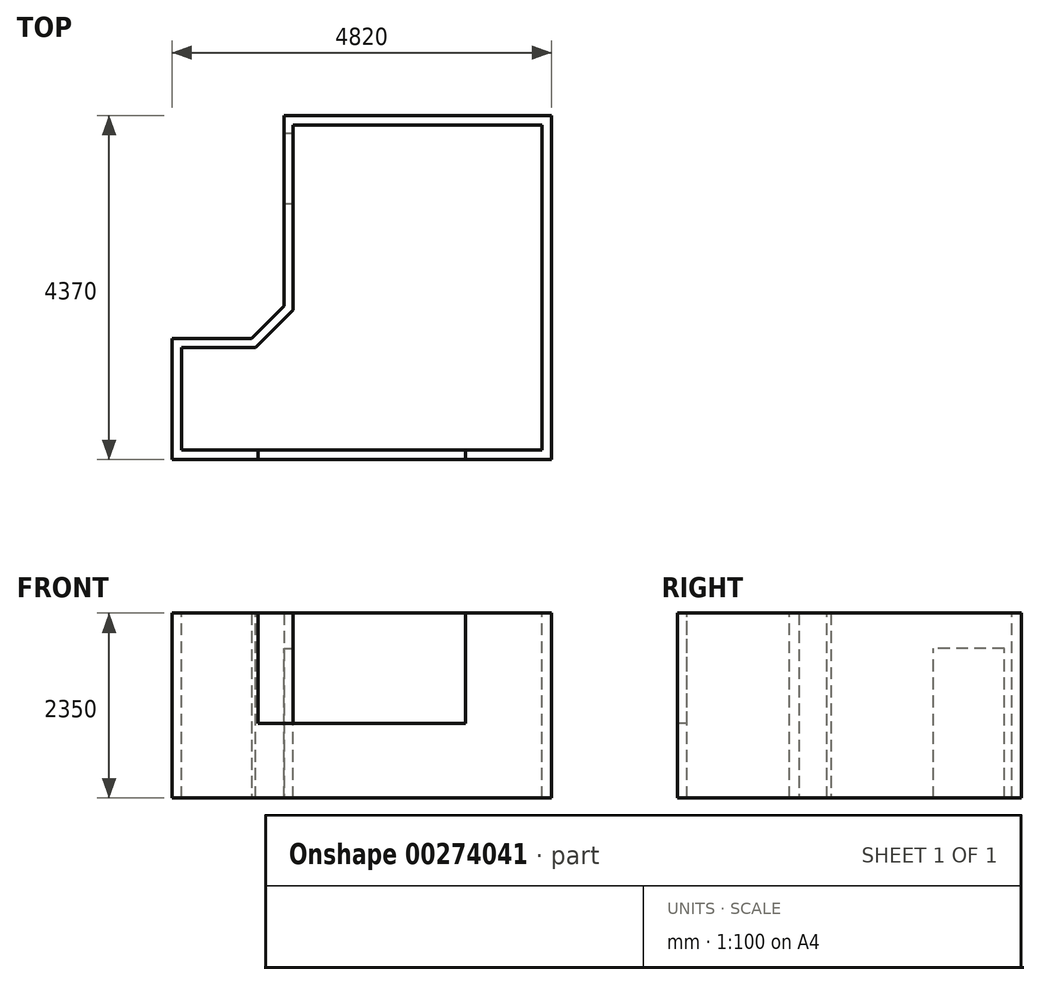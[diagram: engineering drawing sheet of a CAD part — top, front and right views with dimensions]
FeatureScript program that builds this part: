
annotation { "Feature Type Name" : "Feature", "Feature Type Description" : "" }
export const myFeature = defineFeature(function(context is Context, id is Id, definition is map)
    precondition{}
    {
        {
            var Q0;
            Q0=qCreatedBy(makeId("Top.planeOp"),FACE);
            var sketch = newSketch(context, id + "F0", { "sketchPlane" : qUnion([Q0])});
            skLineSegment(sketch, "E0", {"start": v(-2410, -1135) * mm, "end": v(-2410, -2675) * mm});
            skLineSegment(sketch, "E1", {"start": v(-2410, -2675) * mm, "end": v(2410, -2675) * mm});
            skLineSegment(sketch, "E2", {"start": v(2410, -2675) * mm, "end": v(2410, 1695) * mm});
            skLineSegment(sketch, "E3", {"start": v(2410, 1695) * mm, "end": v(-990, 1695) * mm});
            skLineSegment(sketch, "E4", {"start": v(-990, 1695) * mm, "end": v(-990, -725.9) * mm});
            skLineSegment(sketch, "E5", {"start": v(-990, -725.9) * mm, "end": v(-1399.1, -1135) * mm});
            skLineSegment(sketch, "E6", {"start": v(-1399.1, -1135) * mm, "end": v(-2410, -1135) * mm});
            skSolve(sketch);
        }
        {
            var Q0;
            Q0=qSketchRegion(id+"F0",true);
            extrude(context, id + "F1", {"entities" : qUnion([Q0]), "depth" : 2350 * mm});
        }
        {
            var Q0;
            Q0=makeQuery(id+"F1.opExtrude","CAP_FACE",FACE,{"disambiguationData":[OSD([sQuery(id+"F0.wireOp",EDGE,"E0"),sQuery(id+"F0.wireOp",EDGE,"E1"),sQuery(id+"F0.wireOp",EDGE,"E2"),sQuery(id+"F0.wireOp",EDGE,"E3"),sQuery(id+"F0.wireOp",EDGE,"E4"),sQuery(id+"F0.wireOp",EDGE,"E5"),sQuery(id+"F0.wireOp",EDGE,"E6")])],"isStart":false});
            var sketch = newSketch(context, id + "F2", { "sketchPlane" : qUnion([Q0])});
            skLineSegment(sketch, "E7", {"start": v(-2290, -1255) * mm, "end": v(-2290, -2555) * mm});
            skLineSegment(sketch, "E8", {"start": v(-2290, -2555) * mm, "end": v(2290, -2555) * mm});
            skLineSegment(sketch, "E9", {"start": v(2290, -2555) * mm, "end": v(2290, 1575) * mm});
            skLineSegment(sketch, "E10", {"start": v(2290, 1575) * mm, "end": v(-870, 1575) * mm});
            skLineSegment(sketch, "E11", {"start": v(-870, 1575) * mm, "end": v(-870, -775.6) * mm});
            skLineSegment(sketch, "E12", {"start": v(-870, -775.6) * mm, "end": v(-1349.4, -1255) * mm});
            skLineSegment(sketch, "E13", {"start": v(-1349.4, -1255) * mm, "end": v(-2290, -1255) * mm});
            skSolve(sketch);
        }
        {
            var Q0;
            Q0 = qSketchRegion(id + "F2", true);
            extrude(context, id + "F3", {"entities" : qUnion([Q0]), "operationType" : NewBodyOperationType.REMOVE, "endBound" : BoundingType.THROUGH_ALL, "oppositeDirection" : true, "depth" : 25 * mm});
        }
        {
            var Q0;
            Q0=makeQuery(id+"F1.opExtrude","SWEPT_FACE",FACE,{"disambiguationData":[OSD([sQuery(id+"F0.wireOp",EDGE,"E1")])]});
            var sketch = newSketch(context, id + "F4", { "sketchPlane" : qUnion([Q0])});
            skLineSegment(sketch, "E14.bottom", {"start": v(-1320, 2350) * mm, "end": v(1320, 2350) * mm});
            skLineSegment(sketch, "E14.top", {"start": v(-1320, 950) * mm, "end": v(1320, 950) * mm});
            skLineSegment(sketch, "E14.left", {"start": v(-1320, 2350) * mm, "end": v(-1320, 950) * mm});
            skLineSegment(sketch, "E14.right", {"start": v(1320, 2350) * mm, "end": v(1320, 950) * mm});
            skSolve(sketch);
        }
        {
            var Q0;
            Q0 = qSketchRegion(id + "F4", true);
            extrude(context, id + "F5", {"entities" : qUnion([Q0]), "operationType" : NewBodyOperationType.REMOVE, "endBound" : BoundingType.UP_TO_NEXT, "oppositeDirection" : true, "depth" : 25 * mm});
        }
        {
            var Q0;
            Q0=makeQuery(id+"F3.boolean.opBoolean","COPY",FACE,{"derivedFrom":makeQuery(id+"F3.opExtrude","SWEPT_FACE",FACE,{"disambiguationData":[OSD([sQuery(id+"F2.wireOp",EDGE,"E11")])]})});
            var sketch = newSketch(context, id + "F6", { "sketchPlane" : qUnion([Q0])});
            skLineSegment(sketch, "E15.bottom", {"start": v(575, 1900) * mm, "end": v(1475, 1900) * mm});
            skLineSegment(sketch, "E15.top", {"start": v(575, 0) * mm, "end": v(1475, 0) * mm});
            skLineSegment(sketch, "E15.left", {"start": v(575, 1900) * mm, "end": v(575, 0) * mm});
            skLineSegment(sketch, "E15.right", {"start": v(1475, 1900) * mm, "end": v(1475, 0) * mm});
            skSolve(sketch);
        }
        {
            var Q0;
            Q0 = qSketchRegion(id + "F6", true);
            extrude(context, id + "F7", {"entities" : qUnion([Q0]), "operationType" : NewBodyOperationType.REMOVE, "endBound" : BoundingType.UP_TO_NEXT, "oppositeDirection" : true, "depth" : 25 * mm});
        }
    });
